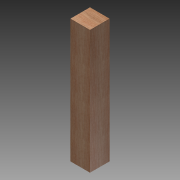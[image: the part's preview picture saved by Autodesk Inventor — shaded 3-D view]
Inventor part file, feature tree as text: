
AUTODESK INVENTOR PART (.ipt)
format: ipt  version: 2015 (Build 190159000, 159)  size: 86,528 bytes
history: native  units: in
note: dims shown in document units (in); Inventor stores cm internally (conversion verified against a paired STEP export)
features: other x2, extrude x1, sketch x1
ambient origin geometry x8: Origin, YZ Plane, XZ Plane, XY Plane, X Axis, Y Axis, Z Axis, Center Point
bodies: Solid1 (feature_tree)
feature tree (4):
  extrude  "Extrusion1"  Depth=38.0in TaperAngle=0.0deg
  other  "Work Axis1"
  sketch  "Sketch1"  dims[d0=6.0in d1=38.0in d2=0.0in]
  other  "Work Point1"
